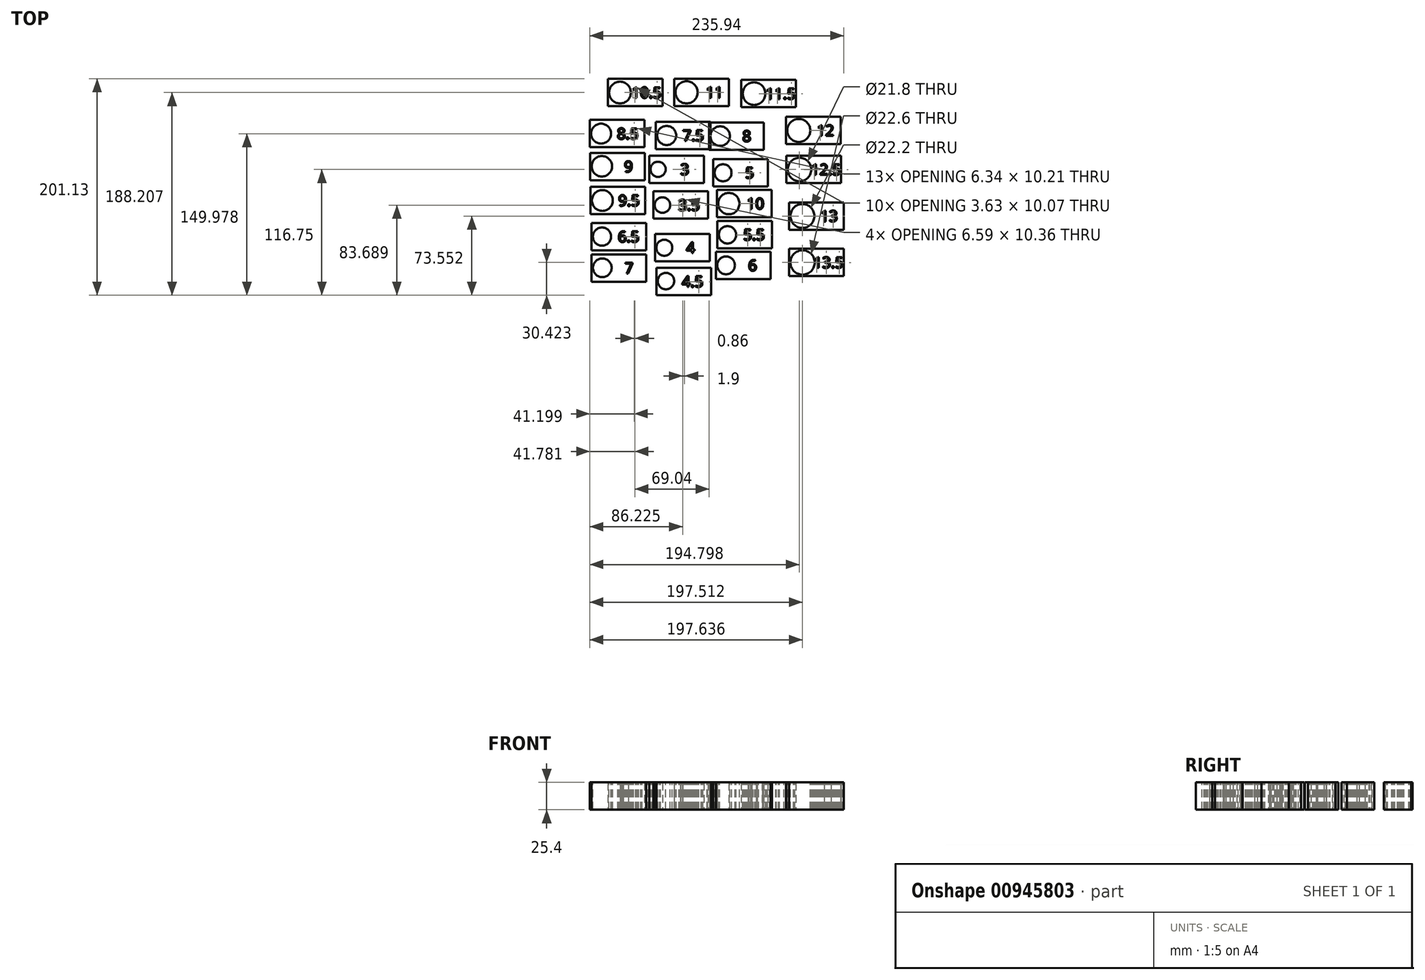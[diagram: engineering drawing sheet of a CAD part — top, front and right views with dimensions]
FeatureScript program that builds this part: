
annotation { "Feature Type Name" : "Feature", "Feature Type Description" : "" }
export const myFeature = defineFeature(function(context is Context, id is Id, definition is map)
    precondition{}
    {
        {
            var Q0;
            Q0=makeQuery(id+"FK1q33cBMZMaRjc_2.opExtrude","CAP_FACE",FACE,{"disambiguationData":[OSD([sQuery(id+"Ff8Uq9xGrrkUuTS_2.wireOp",EDGE,"LQ6pOcAo-RqI5-iYAm-z19J-XkjqRddOA0Lw.bottom"),sQuery(id+"Ff8Uq9xGrrkUuTS_2.wireOp",EDGE,"LQ6pOcAo-RqI5-iYAm-z19J-XkjqRddOA0Lw.top"),sQuery(id+"Ff8Uq9xGrrkUuTS_2.wireOp",EDGE,"LQ6pOcAo-RqI5-iYAm-z19J-XkjqRddOA0Lw.left"),sQuery(id+"Ff8Uq9xGrrkUuTS_2.wireOp",EDGE,"LQ6pOcAo-RqI5-iYAm-z19J-XkjqRddOA0Lw.right")])],"isStart":false});
            var sketch = newSketch(context, id + "F0", { "sketchPlane" : qUnion([Q0])});
            skText(sketch, "E0", { "text": "4", "fontName": "OpenSans-Regular.ttf"});
            const initialGuessF0  = {"E0": [-0.04926, -0.00195, 1, 0, 0.01413]};
            skSetInitialGuess(sketch, initialGuessF0);
            skSolve(sketch);
        }
        {
            var Q0;
            Q0=qCreatedBy(makeId("Top.planeOp"),FACE);
            var sketch = newSketch(context, id + "F1", { "sketchPlane" : qUnion([Q0])});
            skLineSegment(sketch, "E1.bottom", {"start": v(-19.08, 51.73) * mm, "end": v(31.72, 51.73) * mm});
            skLineSegment(sketch, "E1.top", {"start": v(-19.08, 26.33) * mm, "end": v(31.72, 26.33) * mm});
            skLineSegment(sketch, "E1.left", {"start": v(-19.08, 51.73) * mm, "end": v(-19.08, 26.33) * mm});
            skLineSegment(sketch, "E1.right", {"start": v(31.72, 51.73) * mm, "end": v(31.72, 26.33) * mm});
            skSolve(sketch);
        }
        {
            var Q0;
            Q0=qCreatedBy(makeId("Top.planeOp"),FACE);
            var sketch = newSketch(context, id + "F2", { "sketchPlane" : qUnion([Q0])});
            skLineSegment(sketch, "E2.bottom", {"start": v(-15.26, 18.54) * mm, "end": v(35.54, 18.54) * mm});
            skLineSegment(sketch, "E2.top", {"start": v(-15.26, -6.86) * mm, "end": v(35.54, -6.86) * mm});
            skLineSegment(sketch, "E2.left", {"start": v(-15.26, 18.54) * mm, "end": v(-15.26, -6.86) * mm});
            skLineSegment(sketch, "E2.right", {"start": v(35.54, 18.54) * mm, "end": v(35.54, -6.86) * mm});
            skSolve(sketch);
        }
        {
            var Q0;
            Q0=qCreatedBy(makeId("Top.planeOp"),FACE);
            var sketch = newSketch(context, id + "F3", { "sketchPlane" : qUnion([Q0])});
            skLineSegment(sketch, "E3.bottom", {"start": v(-13.72, -20.97) * mm, "end": v(37.08, -20.97) * mm});
            skLineSegment(sketch, "E3.top", {"start": v(-13.72, -46.37) * mm, "end": v(37.08, -46.37) * mm});
            skLineSegment(sketch, "E3.left", {"start": v(-13.72, -20.97) * mm, "end": v(-13.72, -46.37) * mm});
            skLineSegment(sketch, "E3.right", {"start": v(37.08, -20.97) * mm, "end": v(37.08, -46.37) * mm});
            skSolve(sketch);
        }
        {
            var Q0;
            Q0=qCreatedBy(makeId("Top.planeOp"),FACE);
            var sketch = newSketch(context, id + "F4", { "sketchPlane" : qUnion([Q0])});
            skLineSegment(sketch, "E4.bottom", {"start": v(-12.42, -52.5) * mm, "end": v(38.38, -52.5) * mm});
            skLineSegment(sketch, "E4.top", {"start": v(-12.42, -77.9) * mm, "end": v(38.38, -77.9) * mm});
            skLineSegment(sketch, "E4.left", {"start": v(-12.42, -52.5) * mm, "end": v(-12.42, -77.9) * mm});
            skLineSegment(sketch, "E4.right", {"start": v(38.38, -52.5) * mm, "end": v(38.38, -77.9) * mm});
            skSolve(sketch);
        }
        {
            var Q0;
            Q0=qCreatedBy(makeId("Top.planeOp"),FACE);
            var sketch = newSketch(context, id + "F5", { "sketchPlane" : qUnion([Q0])});
            skLineSegment(sketch, "E5.bottom", {"start": v(40.46, 48.55) * mm, "end": v(91.26, 48.55) * mm});
            skLineSegment(sketch, "E5.top", {"start": v(40.46, 23.15) * mm, "end": v(91.26, 23.15) * mm});
            skLineSegment(sketch, "E5.left", {"start": v(40.46, 48.55) * mm, "end": v(40.46, 23.15) * mm});
            skLineSegment(sketch, "E5.right", {"start": v(91.26, 48.55) * mm, "end": v(91.26, 23.15) * mm});
            skSolve(sketch);
        }
        {
            var Q0;
            Q0=qCreatedBy(makeId("Top.planeOp"),FACE);
            var sketch = newSketch(context, id + "F6", { "sketchPlane" : qUnion([Q0])});
            skLineSegment(sketch, "E6.bottom", {"start": v(44.33, -8.99) * mm, "end": v(95.13, -8.99) * mm});
            skLineSegment(sketch, "E6.top", {"start": v(44.33, -34.39) * mm, "end": v(95.13, -34.39) * mm});
            skLineSegment(sketch, "E6.left", {"start": v(44.33, -8.99) * mm, "end": v(44.33, -34.39) * mm});
            skLineSegment(sketch, "E6.right", {"start": v(95.13, -8.99) * mm, "end": v(95.13, -34.39) * mm});
            skSolve(sketch);
        }
        {
            var Q0;
            Q0=qCreatedBy(makeId("Top.planeOp"),FACE);
            var sketch = newSketch(context, id + "F7", { "sketchPlane" : qUnion([Q0])});
            skLineSegment(sketch, "E7.bottom", {"start": v(42.82, -37.42) * mm, "end": v(93.62, -37.42) * mm});
            skLineSegment(sketch, "E7.top", {"start": v(42.82, -62.82) * mm, "end": v(93.62, -62.82) * mm});
            skLineSegment(sketch, "E7.left", {"start": v(42.82, -37.42) * mm, "end": v(42.82, -62.82) * mm});
            skLineSegment(sketch, "E7.right", {"start": v(93.62, -37.42) * mm, "end": v(93.62, -62.82) * mm});
            skSolve(sketch);
        }
        {
            var Q0;
            Q0=makeQuery(id+"F1.imprint","IMPRINT",FACE,{"disambiguationData":[TD([[makeQuery(id+"F1.imprint","IMPRINT",EDGE,{"derivedFrom":sQuery(id+"F1.wireOp",EDGE,"E1.bottom")}),-1.0]])]});
            extrude(context, id + "F8", {"entities" : qUnion([Q0]), "depth" : 25.4 * mm, "offsetDistance" : 25.4 * mm});
        }
        {
            var Q0;
            Q0=makeQuery(id+"F5.imprint","IMPRINT",FACE,{"disambiguationData":[TD([[makeQuery(id+"F5.imprint","IMPRINT",EDGE,{"derivedFrom":sQuery(id+"F5.wireOp",EDGE,"E5.bottom")}),-1.0]])]});
            extrude(context, id + "F9", {"entities" : qUnion([Q0]), "depth" : 25.4 * mm, "offsetDistance" : 25.4 * mm});
        }
        {
            var Q0;
            Q0=makeQuery(id+"F2.imprint","IMPRINT",FACE,{"disambiguationData":[TD([[makeQuery(id+"F2.imprint","IMPRINT",EDGE,{"derivedFrom":sQuery(id+"F2.wireOp",EDGE,"E2.bottom")}),-1.0]])]});
            extrude(context, id + "F10", {"entities" : qUnion([Q0]), "depth" : 25.4 * mm, "offsetDistance" : 25.4 * mm});
        }
        {
            var Q0;
            Q0=makeQuery(id+"F6.imprint","IMPRINT",FACE,{"disambiguationData":[TD([[makeQuery(id+"F6.imprint","IMPRINT",EDGE,{"derivedFrom":sQuery(id+"F6.wireOp",EDGE,"E6.bottom")}),-1.0]])]});
            extrude(context, id + "F11", {"entities" : qUnion([Q0]), "depth" : 25.4 * mm, "offsetDistance" : 25.4 * mm});
        }
        {
            var Q0;
            Q0=makeQuery(id+"F3.imprint","IMPRINT",FACE,{"disambiguationData":[TD([[makeQuery(id+"F3.imprint","IMPRINT",EDGE,{"derivedFrom":sQuery(id+"F3.wireOp",EDGE,"E3.bottom")}),-1.0]])]});
            extrude(context, id + "F12", {"entities" : qUnion([Q0]), "depth" : 25.4 * mm, "offsetDistance" : 25.4 * mm});
        }
        {
            var Q0;
            Q0=makeQuery(id+"F7.imprint","IMPRINT",FACE,{"disambiguationData":[TD([[makeQuery(id+"F7.imprint","IMPRINT",EDGE,{"derivedFrom":sQuery(id+"F7.wireOp",EDGE,"E7.bottom")}),-1.0]])]});
            extrude(context, id + "F13", {"entities" : qUnion([Q0]), "depth" : 25.4 * mm, "offsetDistance" : 25.4 * mm});
        }
        {
            var Q0;
            Q0=makeQuery(id+"F4.imprint","IMPRINT",FACE,{"disambiguationData":[TD([[makeQuery(id+"F4.imprint","IMPRINT",EDGE,{"derivedFrom":sQuery(id+"F4.wireOp",EDGE,"E4.bottom")}),-1.0]])]});
            extrude(context, id + "F14", {"entities" : qUnion([Q0]), "depth" : 25.4 * mm, "offsetDistance" : 25.4 * mm});
        }
        {
            var Q0;
            Q0=makeQuery(id+"F8.opExtrude","CAP_FACE",FACE,{"disambiguationData":[OSD([sQuery(id+"F1.wireOp",EDGE,"E1.bottom"),sQuery(id+"F1.wireOp",EDGE,"E1.top"),sQuery(id+"F1.wireOp",EDGE,"E1.left"),sQuery(id+"F1.wireOp",EDGE,"E1.right")])],"isStart":false});
            var sketch = newSketch(context, id + "F15", { "sketchPlane" : qUnion([Q0])});
            skCircle(sketch, "E8", {"center": v(-10.76, 39.03) * mm, "radius": 7.05 * mm});
            skSolve(sketch);
        }
        {
            var Q0;
            Q0=makeQuery(id+"F15.imprint","IMPRINT",FACE,{"disambiguationData":[TD([[makeQuery(id+"F15.imprint","IMPRINT",EDGE,{"derivedFrom":sQuery(id+"F15.wireOp",EDGE,"E8")}),1.0]])]});
            extrude(context, id + "F16", {"entities" : qUnion([Q0]), "operationType" : NewBodyOperationType.REMOVE, "oppositeDirection" : true, "depth" : 25.4 * mm, "offsetDistance" : 25.4 * mm});
        }
        {
            var Q0;
            Q0=makeQuery(id+"F8.opExtrude","CAP_FACE",FACE,{"disambiguationData":[OSD([sQuery(id+"F1.wireOp",EDGE,"E1.bottom"),sQuery(id+"F1.wireOp",EDGE,"E1.top"),sQuery(id+"F1.wireOp",EDGE,"E1.left"),sQuery(id+"F1.wireOp",EDGE,"E1.right")])],"isStart":false});
            var sketch = newSketch(context, id + "F17", { "sketchPlane" : qUnion([Q0])});
            skText(sketch, "E9", { "text": "3", "fontName": "OpenSans-Regular.ttf"});
            const initialGuessF17  = {"E9": [0.00993, 0.03395, 1, 0, 0.01016]};
            skSetInitialGuess(sketch, initialGuessF17);
            skSolve(sketch);
        }
        {
            var Q0;
            Q0=makeQuery(id+"F17.imprint","IMPRINT",FACE,{"disambiguationData":[TD([[makeQuery(id+"F17.imprint","IMPRINT",EDGE,{"derivedFrom":sQuery(id+"F17.wireOp",EDGE,"E9.sketch_text.stroke-0")}),-1.0]])]});
            extrude(context, id + "F18", {"entities" : qUnion([Q0]), "operationType" : NewBodyOperationType.REMOVE, "oppositeDirection" : true, "depth" : 25.4 * mm, "offsetDistance" : 25.4 * mm});
        }
        {
            var Q0;
            Q0=makeQuery(id+"F10.opExtrude","CAP_FACE",FACE,{"disambiguationData":[OSD([sQuery(id+"F2.wireOp",EDGE,"E2.bottom"),sQuery(id+"F2.wireOp",EDGE,"E2.top"),sQuery(id+"F2.wireOp",EDGE,"E2.left"),sQuery(id+"F2.wireOp",EDGE,"E2.right")])],"isStart":false});
            var sketch = newSketch(context, id + "F19", { "sketchPlane" : qUnion([Q0])});
            skCircle(sketch, "E10", {"center": v(-6.74, 5.84) * mm, "radius": 7.25 * mm});
            skSolve(sketch);
        }
        {
            var Q0;
            Q0=makeQuery(id+"F19.imprint","IMPRINT",FACE,{"disambiguationData":[TD([[makeQuery(id+"F19.imprint","IMPRINT",EDGE,{"derivedFrom":sQuery(id+"F19.wireOp",EDGE,"E10")}),1.0]])]});
            extrude(context, id + "F20", {"entities" : qUnion([Q0]), "operationType" : NewBodyOperationType.REMOVE, "oppositeDirection" : true, "depth" : 25.4 * mm, "offsetDistance" : 25.4 * mm});
        }
        {
            var Q0;
            Q0=makeQuery(id+"F10.opExtrude","CAP_FACE",FACE,{"disambiguationData":[OSD([sQuery(id+"F2.wireOp",EDGE,"E2.bottom"),sQuery(id+"F2.wireOp",EDGE,"E2.top"),sQuery(id+"F2.wireOp",EDGE,"E2.left"),sQuery(id+"F2.wireOp",EDGE,"E2.right")])],"isStart":false});
            var sketch = newSketch(context, id + "F21", { "sketchPlane" : qUnion([Q0])});
            skText(sketch, "E11", { "text": "3.5", "fontName": "OpenSans-Regular.ttf"});
            const initialGuessF21  = {"E11": [0.00803, 0.00076, 1, 0, 0.01016]};
            skSetInitialGuess(sketch, initialGuessF21);
            skSolve(sketch);
        }
        {
            var Q0;
            Q0 = qSketchRegion(id + "F21", true);
            extrude(context, id + "F22", {"entities" : qUnion([Q0]), "operationType" : NewBodyOperationType.REMOVE, "oppositeDirection" : true, "depth" : 25.4 * mm, "offsetDistance" : 25.4 * mm});
        }
        {
            var Q0;
            Q0=makeQuery(id+"F12.opExtrude","CAP_FACE",FACE,{"disambiguationData":[OSD([sQuery(id+"F3.wireOp",EDGE,"E3.bottom"),sQuery(id+"F3.wireOp",EDGE,"E3.top"),sQuery(id+"F3.wireOp",EDGE,"E3.left"),sQuery(id+"F3.wireOp",EDGE,"E3.right")])],"isStart":false});
            var sketch = newSketch(context, id + "F23", { "sketchPlane" : qUnion([Q0])});
            skCircle(sketch, "E12", {"center": v(-5, -33.82) * mm, "radius": 7.45 * mm});
            skSolve(sketch);
        }
        {
            var Q0;
            Q0=makeQuery(id+"F23.imprint","IMPRINT",FACE,{"disambiguationData":[TD([[makeQuery(id+"F23.imprint","IMPRINT",EDGE,{"derivedFrom":sQuery(id+"F23.wireOp",EDGE,"E12")}),1.0]])]});
            extrude(context, id + "F24", {"entities" : qUnion([Q0]), "operationType" : NewBodyOperationType.REMOVE, "oppositeDirection" : true, "depth" : 25.4 * mm, "offsetDistance" : 25.4 * mm});
        }
        {
            var Q0;
            Q0=makeQuery(id+"F12.opExtrude","CAP_FACE",FACE,{"disambiguationData":[OSD([sQuery(id+"F3.wireOp",EDGE,"E3.bottom"),sQuery(id+"F3.wireOp",EDGE,"E3.top"),sQuery(id+"F3.wireOp",EDGE,"E3.left"),sQuery(id+"F3.wireOp",EDGE,"E3.right")])],"isStart":false});
            var sketch = newSketch(context, id + "F25", { "sketchPlane" : qUnion([Q0])});
            skText(sketch, "E13", { "text": "4", "fontName": "OpenSans-Regular.ttf"});
            const initialGuessF25  = {"E13": [0.0154, -0.03875, 1, 0, 0.01016]};
            skSetInitialGuess(sketch, initialGuessF25);
            skSolve(sketch);
        }
        {
            var Q0;
            Q0=makeQuery(id+"F25.imprint","IMPRINT",FACE,{"disambiguationData":[TD([[makeQuery(id+"F25.imprint","IMPRINT",EDGE,{"derivedFrom":sQuery(id+"F25.wireOp",EDGE,"E13.sketch_text.stroke-0")}),-1.0]])]});
            extrude(context, id + "F26", {"entities" : qUnion([Q0]), "operationType" : NewBodyOperationType.REMOVE, "oppositeDirection" : true, "depth" : 25.4 * mm, "offsetDistance" : 25.4 * mm});
        }
        {
            var Q0;
            Q0=makeQuery(id+"F14.opExtrude","CAP_FACE",FACE,{"disambiguationData":[OSD([sQuery(id+"F4.wireOp",EDGE,"E4.bottom"),sQuery(id+"F4.wireOp",EDGE,"E4.top"),sQuery(id+"F4.wireOp",EDGE,"E4.left"),sQuery(id+"F4.wireOp",EDGE,"E4.right")])],"isStart":false});
            var sketch = newSketch(context, id + "F27", { "sketchPlane" : qUnion([Q0])});
            skCircle(sketch, "E14", {"center": v(-3.5, -64.73) * mm, "radius": 7.65 * mm});
            skSolve(sketch);
        }
        {
            var Q0;
            Q0=makeQuery(id+"F27.imprint","IMPRINT",FACE,{"disambiguationData":[TD([[makeQuery(id+"F27.imprint","IMPRINT",EDGE,{"derivedFrom":sQuery(id+"F27.wireOp",EDGE,"E14")}),1.0]])]});
            extrude(context, id + "F28", {"entities" : qUnion([Q0]), "operationType" : NewBodyOperationType.REMOVE, "oppositeDirection" : true, "depth" : 25.4 * mm, "offsetDistance" : 25.4 * mm});
        }
        {
            var Q0;
            Q0=makeQuery(id+"F14.opExtrude","CAP_FACE",FACE,{"disambiguationData":[OSD([sQuery(id+"F4.wireOp",EDGE,"E4.bottom"),sQuery(id+"F4.wireOp",EDGE,"E4.top"),sQuery(id+"F4.wireOp",EDGE,"E4.left"),sQuery(id+"F4.wireOp",EDGE,"E4.right")])],"isStart":false});
            var sketch = newSketch(context, id + "F29", { "sketchPlane" : qUnion([Q0])});
            skText(sketch, "E15", { "text": "4.5", "fontName": "OpenSans-Regular.ttf"});
            const initialGuessF29  = {"E15": [0.01127, -0.07027, 1, 0, 0.01016]};
            skSetInitialGuess(sketch, initialGuessF29);
            skSolve(sketch);
        }
        {
            var Q0;
            Q0 = qSketchRegion(id + "F29", true);
            extrude(context, id + "F30", {"entities" : qUnion([Q0]), "operationType" : NewBodyOperationType.REMOVE, "oppositeDirection" : true, "depth" : 25.4 * mm, "offsetDistance" : 25.4 * mm});
        }
        {
            var Q0;
            Q0=makeQuery(id+"F9.opExtrude","CAP_FACE",FACE,{"disambiguationData":[OSD([sQuery(id+"F5.wireOp",EDGE,"E5.bottom"),sQuery(id+"F5.wireOp",EDGE,"E5.top"),sQuery(id+"F5.wireOp",EDGE,"E5.left"),sQuery(id+"F5.wireOp",EDGE,"E5.right")])],"isStart":false});
            var sketch = newSketch(context, id + "F31", { "sketchPlane" : qUnion([Q0])});
            skCircle(sketch, "E16", {"center": v(49.58, 35.83) * mm, "radius": 7.85 * mm});
            skSolve(sketch);
        }
        {
            var Q0;
            Q0=makeQuery(id+"F31.imprint","IMPRINT",FACE,{"disambiguationData":[TD([[makeQuery(id+"F31.imprint","IMPRINT",EDGE,{"derivedFrom":sQuery(id+"F31.wireOp",EDGE,"E16")}),1.0]])]});
            extrude(context, id + "F32", {"entities" : qUnion([Q0]), "operationType" : NewBodyOperationType.REMOVE, "oppositeDirection" : true, "depth" : 25.4 * mm, "offsetDistance" : 25.4 * mm});
        }
        {
            var Q0;
            Q0=makeQuery(id+"F9.opExtrude","CAP_FACE",FACE,{"disambiguationData":[OSD([sQuery(id+"F5.wireOp",EDGE,"E5.bottom"),sQuery(id+"F5.wireOp",EDGE,"E5.top"),sQuery(id+"F5.wireOp",EDGE,"E5.left"),sQuery(id+"F5.wireOp",EDGE,"E5.right")])],"isStart":false});
            var sketch = newSketch(context, id + "F33", { "sketchPlane" : qUnion([Q0])});
            skText(sketch, "E17", { "text": "5", "fontName": "OpenSans-Regular.ttf"});
            const initialGuessF33  = {"E17": [0.07013, 0.03077, 1, 0, 0.01016]};
            skSetInitialGuess(sketch, initialGuessF33);
            skSolve(sketch);
        }
        {
            var Q0;
            Q0 = qSketchRegion(id + "F33", true);
            extrude(context, id + "F34", {"entities" : qUnion([Q0]), "operationType" : NewBodyOperationType.REMOVE, "oppositeDirection" : true, "depth" : 25.4 * mm, "offsetDistance" : 25.4 * mm});
        }
        {
            var Q0;
            Q0=makeQuery(id+"F11.opExtrude","CAP_FACE",FACE,{"disambiguationData":[OSD([sQuery(id+"F6.wireOp",EDGE,"E6.bottom"),sQuery(id+"F6.wireOp",EDGE,"E6.top"),sQuery(id+"F6.wireOp",EDGE,"E6.left"),sQuery(id+"F6.wireOp",EDGE,"E6.right")])],"isStart":false});
            var sketch = newSketch(context, id + "F35", { "sketchPlane" : qUnion([Q0])});
            skCircle(sketch, "E18", {"center": v(53.65, -21.76) * mm, "radius": 8.05 * mm});
            skSolve(sketch);
        }
        {
            var Q0;
            Q0=makeQuery(id+"F35.imprint","IMPRINT",FACE,{"disambiguationData":[TD([[makeQuery(id+"F35.imprint","IMPRINT",EDGE,{"derivedFrom":sQuery(id+"F35.wireOp",EDGE,"E18")}),1.0]])]});
            extrude(context, id + "F36", {"entities" : qUnion([Q0]), "operationType" : NewBodyOperationType.REMOVE, "oppositeDirection" : true, "depth" : 25.4 * mm, "offsetDistance" : 25.4 * mm});
        }
        {
            var Q0;
            Q0=makeQuery(id+"F11.opExtrude","CAP_FACE",FACE,{"disambiguationData":[OSD([sQuery(id+"F6.wireOp",EDGE,"E6.bottom"),sQuery(id+"F6.wireOp",EDGE,"E6.top"),sQuery(id+"F6.wireOp",EDGE,"E6.left"),sQuery(id+"F6.wireOp",EDGE,"E6.right")])],"isStart":false});
            var sketch = newSketch(context, id + "F37", { "sketchPlane" : qUnion([Q0])});
            skText(sketch, "E19", { "text": "5.5\n", "fontName": "OpenSans-Regular.ttf"});
            const initialGuessF37  = {"E19": [0.06842, -0.02677, 1, 0, 0.01016]};
            skSetInitialGuess(sketch, initialGuessF37);
            skSolve(sketch);
        }
        {
            var Q0;
            Q0=makeQuery(id+"F37.imprint","IMPRINT",FACE,{"disambiguationData":[TD([[makeQuery(id+"F37.imprint","IMPRINT",EDGE,{"derivedFrom":sQuery(id+"F37.wireOp",EDGE,"E19.sketch_text.stroke-27")}),-1.0]])]});
            var Q1;
            Q1 = qSketchRegion(id + "F37", true);
            extrude(context, id + "F38", {"entities" : qUnion([Q0, Q1]), "operationType" : NewBodyOperationType.REMOVE, "oppositeDirection" : true, "depth" : 25.4 * mm, "offsetDistance" : 25.4 * mm});
        }
        {
            var Q0;
            Q0=makeQuery(id+"F13.opExtrude","CAP_FACE",FACE,{"disambiguationData":[OSD([sQuery(id+"F7.wireOp",EDGE,"E7.bottom"),sQuery(id+"F7.wireOp",EDGE,"E7.top"),sQuery(id+"F7.wireOp",EDGE,"E7.left"),sQuery(id+"F7.wireOp",EDGE,"E7.right")])],"isStart":false});
            var sketch = newSketch(context, id + "F39", { "sketchPlane" : qUnion([Q0])});
            skCircle(sketch, "E20", {"center": v(52.34, -50.13) * mm, "radius": 8.25 * mm});
            skSolve(sketch);
        }
        {
            var Q0;
            Q0=makeQuery(id+"F39.imprint","IMPRINT",FACE,{"disambiguationData":[TD([[makeQuery(id+"F39.imprint","IMPRINT",EDGE,{"derivedFrom":sQuery(id+"F39.wireOp",EDGE,"E20")}),1.0]])]});
            extrude(context, id + "F40", {"entities" : qUnion([Q0]), "operationType" : NewBodyOperationType.REMOVE, "oppositeDirection" : true, "depth" : 25.4 * mm, "offsetDistance" : 25.4 * mm});
        }
        {
            var Q0;
            Q0=makeQuery(id+"F13.opExtrude","CAP_FACE",FACE,{"disambiguationData":[OSD([sQuery(id+"F7.wireOp",EDGE,"E7.bottom"),sQuery(id+"F7.wireOp",EDGE,"E7.top"),sQuery(id+"F7.wireOp",EDGE,"E7.left"),sQuery(id+"F7.wireOp",EDGE,"E7.right")])],"isStart":false});
            var sketch = newSketch(context, id + "F41", { "sketchPlane" : qUnion([Q0])});
            skText(sketch, "E21", { "text": "6", "fontName": "OpenSans-Regular.ttf"});
            const initialGuessF41  = {"E21": [0.07295, -0.0552, 1, 0, 0.01016]};
            skSetInitialGuess(sketch, initialGuessF41);
            skSolve(sketch);
        }
        {
            var Q0;
            Q0 = qSketchRegion(id + "F41", true);
            extrude(context, id + "F42", {"entities" : qUnion([Q0]), "operationType" : NewBodyOperationType.REMOVE, "oppositeDirection" : true, "depth" : 25.4 * mm, "offsetDistance" : 25.4 * mm});
        }
        {
            var Q0;
            Q0=qCreatedBy(makeId("Top.planeOp"),FACE);
            var sketch = newSketch(context, id + "F43", { "sketchPlane" : qUnion([Q0])});
            skLineSegment(sketch, "E22.bottom", {"start": v(-72.58, -10.77) * mm, "end": v(-21.78, -10.77) * mm});
            skLineSegment(sketch, "E22.top", {"start": v(-72.58, -36.17) * mm, "end": v(-21.78, -36.17) * mm});
            skLineSegment(sketch, "E22.left", {"start": v(-72.58, -10.77) * mm, "end": v(-72.58, -36.17) * mm});
            skLineSegment(sketch, "E22.right", {"start": v(-21.78, -10.77) * mm, "end": v(-21.78, -36.17) * mm});
            skSolve(sketch);
        }
        {
            var Q0;
            Q0=qCreatedBy(makeId("Top.planeOp"),FACE);
            var sketch = newSketch(context, id + "F44", { "sketchPlane" : qUnion([Q0])});
            skLineSegment(sketch, "E23.bottom", {"start": v(-72.53, -40) * mm, "end": v(-21.73, -40) * mm});
            skLineSegment(sketch, "E23.top", {"start": v(-72.53, -65.4) * mm, "end": v(-21.73, -65.4) * mm});
            skLineSegment(sketch, "E23.left", {"start": v(-72.53, -40) * mm, "end": v(-72.53, -65.4) * mm});
            skLineSegment(sketch, "E23.right", {"start": v(-21.73, -40) * mm, "end": v(-21.73, -65.4) * mm});
            skSolve(sketch);
        }
        {
            var Q0;
            Q0=qCreatedBy(makeId("Top.planeOp"),FACE);
            var sketch = newSketch(context, id + "F45", { "sketchPlane" : qUnion([Q0])});
            skLineSegment(sketch, "E24.bottom", {"start": v(-12.95, 83.2) * mm, "end": v(37.85, 83.2) * mm});
            skLineSegment(sketch, "E24.top", {"start": v(-12.95, 57.8) * mm, "end": v(37.85, 57.8) * mm});
            skLineSegment(sketch, "E24.left", {"start": v(-12.95, 83.2) * mm, "end": v(-12.95, 57.8) * mm});
            skLineSegment(sketch, "E24.right", {"start": v(37.85, 83.2) * mm, "end": v(37.85, 57.8) * mm});
            skSolve(sketch);
        }
        {
            var Q0;
            Q0=qCreatedBy(makeId("Top.planeOp"),FACE);
            var sketch = newSketch(context, id + "F46", { "sketchPlane" : qUnion([Q0])});
            skLineSegment(sketch, "E25.bottom", {"start": v(36.57, 82.63) * mm, "end": v(87.37, 82.63) * mm});
            skLineSegment(sketch, "E25.top", {"start": v(36.57, 57.23) * mm, "end": v(87.37, 57.23) * mm});
            skLineSegment(sketch, "E25.left", {"start": v(36.57, 82.63) * mm, "end": v(36.57, 57.23) * mm});
            skLineSegment(sketch, "E25.right", {"start": v(87.37, 82.63) * mm, "end": v(87.37, 57.23) * mm});
            skSolve(sketch);
        }
        {
            var Q0;
            Q0=makeQuery(id+"F43.imprint","IMPRINT",FACE,{"disambiguationData":[TD([[makeQuery(id+"F43.imprint","IMPRINT",EDGE,{"derivedFrom":sQuery(id+"F43.wireOp",EDGE,"E22.bottom")}),-1.0]])]});
            extrude(context, id + "F47", {"entities" : qUnion([Q0]), "depth" : 25.4 * mm, "offsetDistance" : 25.4 * mm});
        }
        {
            var Q0;
            Q0=makeQuery(id+"F44.imprint","IMPRINT",FACE,{"disambiguationData":[TD([[makeQuery(id+"F44.imprint","IMPRINT",EDGE,{"derivedFrom":sQuery(id+"F44.wireOp",EDGE,"E23.bottom")}),-1.0]])]});
            extrude(context, id + "F48", {"entities" : qUnion([Q0]), "depth" : 25.4 * mm, "offsetDistance" : 25.4 * mm});
        }
        {
            var Q0;
            Q0=makeQuery(id+"F45.imprint","IMPRINT",FACE,{"disambiguationData":[TD([[makeQuery(id+"F45.imprint","IMPRINT",EDGE,{"derivedFrom":sQuery(id+"F45.wireOp",EDGE,"E24.bottom")}),-1.0]])]});
            extrude(context, id + "F49", {"entities" : qUnion([Q0]), "depth" : 25.4 * mm, "offsetDistance" : 25.4 * mm});
        }
        {
            var Q0;
            Q0=makeQuery(id+"F46.imprint","IMPRINT",FACE,{"disambiguationData":[TD([[makeQuery(id+"F46.imprint","IMPRINT",EDGE,{"derivedFrom":sQuery(id+"F46.wireOp",EDGE,"E25.bottom")}),-1.0]])]});
            extrude(context, id + "F50", {"entities" : qUnion([Q0]), "depth" : 25.4 * mm, "offsetDistance" : 25.4 * mm});
        }
        {
            var Q0;
            Q0=makeQuery(id+"F47.opExtrude","CAP_FACE",FACE,{"disambiguationData":[OSD([sQuery(id+"F43.wireOp",EDGE,"E22.bottom"),sQuery(id+"F43.wireOp",EDGE,"E22.top"),sQuery(id+"F43.wireOp",EDGE,"E22.left"),sQuery(id+"F43.wireOp",EDGE,"E22.right")])],"isStart":false});
            var sketch = newSketch(context, id + "F51", { "sketchPlane" : qUnion([Q0])});
            skCircle(sketch, "E26", {"center": v(-62.86, -23.47) * mm, "radius": 8.45 * mm});
            skSolve(sketch);
        }
        {
            var Q0;
            Q0=makeQuery(id+"F51.imprint","IMPRINT",FACE,{"disambiguationData":[TD([[makeQuery(id+"F51.imprint","IMPRINT",EDGE,{"derivedFrom":sQuery(id+"F51.wireOp",EDGE,"E26")}),1.0]])]});
            extrude(context, id + "F52", {"entities" : qUnion([Q0]), "operationType" : NewBodyOperationType.REMOVE, "oppositeDirection" : true, "depth" : 25.4 * mm, "offsetDistance" : 25.4 * mm});
        }
        {
            var Q0;
            Q0=makeQuery(id+"F47.opExtrude","CAP_FACE",FACE,{"disambiguationData":[OSD([sQuery(id+"F43.wireOp",EDGE,"E22.bottom"),sQuery(id+"F43.wireOp",EDGE,"E22.top"),sQuery(id+"F43.wireOp",EDGE,"E22.left"),sQuery(id+"F43.wireOp",EDGE,"E22.right")])],"isStart":false});
            var sketch = newSketch(context, id + "F53", { "sketchPlane" : qUnion([Q0])});
            skText(sketch, "E27", { "text": "6.5", "fontName": "OpenSans-Regular.ttf"});
            const initialGuessF53  = {"E27": [-0.0481, -0.02855, 1, 0, 0.01016]};
            skSetInitialGuess(sketch, initialGuessF53);
            skSolve(sketch);
        }
        {
            var Q0;
            Q0 = qSketchRegion(id + "F53", true);
            extrude(context, id + "F54", {"entities" : qUnion([Q0]), "operationType" : NewBodyOperationType.REMOVE, "oppositeDirection" : true, "depth" : 25.4 * mm, "offsetDistance" : 25.4 * mm});
        }
        {
            var Q0;
            Q0=makeQuery(id+"F48.opExtrude","CAP_FACE",FACE,{"disambiguationData":[OSD([sQuery(id+"F44.wireOp",EDGE,"E23.bottom"),sQuery(id+"F44.wireOp",EDGE,"E23.top"),sQuery(id+"F44.wireOp",EDGE,"E23.left"),sQuery(id+"F44.wireOp",EDGE,"E23.right")])],"isStart":false});
            var sketch = newSketch(context, id + "F55", { "sketchPlane" : qUnion([Q0])});
            skCircle(sketch, "E28", {"center": v(-62.62, -52.42) * mm, "radius": 8.65 * mm});
            skSolve(sketch);
        }
        {
            var Q0;
            Q0=makeQuery(id+"F55.imprint","IMPRINT",FACE,{"disambiguationData":[TD([[makeQuery(id+"F55.imprint","IMPRINT",EDGE,{"derivedFrom":sQuery(id+"F55.wireOp",EDGE,"E28")}),1.0]])]});
            extrude(context, id + "F56", {"entities" : qUnion([Q0]), "operationType" : NewBodyOperationType.REMOVE, "oppositeDirection" : true, "depth" : 25.4 * mm, "offsetDistance" : 25.4 * mm});
        }
        {
            var Q0;
            Q0=makeQuery(id+"F48.opExtrude","CAP_FACE",FACE,{"disambiguationData":[OSD([sQuery(id+"F44.wireOp",EDGE,"E23.bottom"),sQuery(id+"F44.wireOp",EDGE,"E23.top"),sQuery(id+"F44.wireOp",EDGE,"E23.left"),sQuery(id+"F44.wireOp",EDGE,"E23.right")])],"isStart":false});
            var sketch = newSketch(context, id + "F57", { "sketchPlane" : qUnion([Q0])});
            skText(sketch, "E29", { "text": "7", "fontName": "OpenSans-Regular.ttf"});
            const initialGuessF57  = {"E29": [-0.04198, -0.05777, 1, 0, 0.01016]};
            skSetInitialGuess(sketch, initialGuessF57);
            skSolve(sketch);
        }
        {
            var Q0;
            Q0 = qSketchRegion(id + "F57", true);
            extrude(context, id + "F58", {"entities" : qUnion([Q0]), "operationType" : NewBodyOperationType.REMOVE, "oppositeDirection" : true, "depth" : 25.4 * mm, "offsetDistance" : 25.4 * mm});
        }
        {
            var Q0;
            Q0=makeQuery(id+"F49.opExtrude","CAP_FACE",FACE,{"disambiguationData":[OSD([sQuery(id+"F45.wireOp",EDGE,"E24.bottom"),sQuery(id+"F45.wireOp",EDGE,"E24.top"),sQuery(id+"F45.wireOp",EDGE,"E24.left"),sQuery(id+"F45.wireOp",EDGE,"E24.right")])],"isStart":false});
            var sketch = newSketch(context, id + "F59", { "sketchPlane" : qUnion([Q0])});
            skCircle(sketch, "E30", {"center": v(-2.83, 70.46) * mm, "radius": 8.85 * mm});
            skSolve(sketch);
        }
        {
            var Q0;
            Q0=makeQuery(id+"F59.imprint","IMPRINT",FACE,{"disambiguationData":[TD([[makeQuery(id+"F59.imprint","IMPRINT",EDGE,{"derivedFrom":sQuery(id+"F59.wireOp",EDGE,"E30")}),1.0]])]});
            extrude(context, id + "F60", {"entities" : qUnion([Q0]), "operationType" : NewBodyOperationType.ADD, "depth" : 25.4 * mm, "offsetDistance" : 25.4 * mm});
        }
        {
            var Q0;
            Q0=makeQuery(id+"F60.opExtrude","CAP_FACE",FACE,{"disambiguationData":[OSD([sQuery(id+"F59.wireOp",EDGE,"E30")])],"isStart":false});
            extrude(context, id + "F61", {"entities" : qUnion([Q0]), "operationType" : NewBodyOperationType.REMOVE, "oppositeDirection" : true, "depth" : 50.8 * mm, "offsetDistance" : 25.4 * mm});
        }
        {
            var Q0;
            Q0=makeQuery(id+"F49.opExtrude","CAP_FACE",FACE,{"disambiguationData":[OSD([sQuery(id+"F45.wireOp",EDGE,"E24.bottom"),sQuery(id+"F45.wireOp",EDGE,"E24.top"),sQuery(id+"F45.wireOp",EDGE,"E24.left"),sQuery(id+"F45.wireOp",EDGE,"E24.right")])],"isStart":false});
            var sketch = newSketch(context, id + "F62", { "sketchPlane" : qUnion([Q0])});
            skText(sketch, "E31", { "text": "7.5", "fontName": "OpenSans-Regular.ttf"});
            const initialGuessF62  = {"E31": [0.01194, 0.06542, 1, 0, 0.01016]};
            skSetInitialGuess(sketch, initialGuessF62);
            skSolve(sketch);
        }
        {
            var Q0;
            Q0 = qSketchRegion(id + "F62", true);
            extrude(context, id + "F63", {"entities" : qUnion([Q0]), "operationType" : NewBodyOperationType.REMOVE, "oppositeDirection" : true, "depth" : 25.4 * mm, "offsetDistance" : 25.4 * mm});
        }
        {
            var Q0;
            Q0=makeQuery(id+"F50.opExtrude","CAP_FACE",FACE,{"disambiguationData":[OSD([sQuery(id+"F46.wireOp",EDGE,"E25.bottom"),sQuery(id+"F46.wireOp",EDGE,"E25.top"),sQuery(id+"F46.wireOp",EDGE,"E25.left"),sQuery(id+"F46.wireOp",EDGE,"E25.right")])],"isStart":false});
            var sketch = newSketch(context, id + "F64", { "sketchPlane" : qUnion([Q0])});
            skCircle(sketch, "E32", {"center": v(46.9, 69.9) * mm, "radius": 9.05 * mm});
            skSolve(sketch);
        }
        {
            var Q0;
            Q0=makeQuery(id+"F64.imprint","IMPRINT",FACE,{"disambiguationData":[TD([[makeQuery(id+"F64.imprint","IMPRINT",EDGE,{"derivedFrom":sQuery(id+"F64.wireOp",EDGE,"E32")}),1.0]])]});
            extrude(context, id + "F65", {"entities" : qUnion([Q0]), "operationType" : NewBodyOperationType.REMOVE, "oppositeDirection" : true, "depth" : 25.4 * mm, "offsetDistance" : 25.4 * mm});
        }
        {
            var Q0;
            Q0=makeQuery(id+"F50.opExtrude","CAP_FACE",FACE,{"disambiguationData":[OSD([sQuery(id+"F46.wireOp",EDGE,"E25.bottom"),sQuery(id+"F46.wireOp",EDGE,"E25.top"),sQuery(id+"F46.wireOp",EDGE,"E25.left"),sQuery(id+"F46.wireOp",EDGE,"E25.right")])],"isStart":false});
            var sketch = newSketch(context, id + "F66", { "sketchPlane" : qUnion([Q0])});
            skText(sketch, "E33", { "text": "8", "fontName": "OpenSans-Regular.ttf"});
            const initialGuessF66  = {"E33": [0.06751, 0.06485, 1, 0, 0.01016]};
            skSetInitialGuess(sketch, initialGuessF66);
            skSolve(sketch);
        }
        {
            var Q0;
            Q0=makeQuery(id+"F66.imprint","IMPRINT",FACE,{"disambiguationData":[TD([[makeQuery(id+"F66.imprint","IMPRINT",EDGE,{"derivedFrom":sQuery(id+"F66.wireOp",EDGE,"E33.sketch_text.stroke-0")}),-1.0]])]});
            extrude(context, id + "F67", {"entities" : qUnion([Q0]), "operationType" : NewBodyOperationType.REMOVE, "oppositeDirection" : true, "depth" : 25.4 * mm, "offsetDistance" : 25.4 * mm});
        }
        {
            var Q0;
            Q0=qCreatedBy(makeId("Top.planeOp"),FACE);
            var sketch = newSketch(context, id + "F68", { "sketchPlane" : qUnion([Q0])});
            skLineSegment(sketch, "E34.bottom", {"start": v(-74.25, 84.9) * mm, "end": v(-23.45, 84.9) * mm});
            skLineSegment(sketch, "E34.top", {"start": v(-74.25, 59.5) * mm, "end": v(-23.45, 59.5) * mm});
            skLineSegment(sketch, "E34.left", {"start": v(-74.25, 84.9) * mm, "end": v(-74.25, 59.5) * mm});
            skLineSegment(sketch, "E34.right", {"start": v(-23.45, 84.9) * mm, "end": v(-23.45, 59.5) * mm});
            skSolve(sketch);
        }
        {
            var Q0;
            Q0=qCreatedBy(makeId("Top.planeOp"),FACE);
            var sketch = newSketch(context, id + "F69", { "sketchPlane" : qUnion([Q0])});
            skLineSegment(sketch, "E35.bottom", {"start": v(-73.78, 54.3) * mm, "end": v(-22.98, 54.3) * mm});
            skLineSegment(sketch, "E35.top", {"start": v(-73.78, 28.9) * mm, "end": v(-22.98, 28.9) * mm});
            skLineSegment(sketch, "E35.left", {"start": v(-73.78, 54.3) * mm, "end": v(-73.78, 28.9) * mm});
            skLineSegment(sketch, "E35.right", {"start": v(-22.98, 54.3) * mm, "end": v(-22.98, 28.9) * mm});
            skSolve(sketch);
        }
        {
            var Q0;
            Q0=qCreatedBy(makeId("Top.planeOp"),FACE);
            var sketch = newSketch(context, id + "F70", { "sketchPlane" : qUnion([Q0])});
            skLineSegment(sketch, "E36.bottom", {"start": v(-73.54, 22.78) * mm, "end": v(-22.74, 22.78) * mm});
            skLineSegment(sketch, "E36.top", {"start": v(-73.54, -2.62) * mm, "end": v(-22.74, -2.62) * mm});
            skLineSegment(sketch, "E36.left", {"start": v(-73.54, 22.78) * mm, "end": v(-73.54, -2.62) * mm});
            skLineSegment(sketch, "E36.right", {"start": v(-22.74, 22.78) * mm, "end": v(-22.74, -2.62) * mm});
            skSolve(sketch);
        }
        {
            var Q0;
            Q0=qCreatedBy(makeId("Top.planeOp"),FACE);
            var sketch = newSketch(context, id + "F71", { "sketchPlane" : qUnion([Q0])});
            skLineSegment(sketch, "E37.bottom", {"start": v(43.73, 19.92) * mm, "end": v(94.53, 19.92) * mm});
            skLineSegment(sketch, "E37.top", {"start": v(43.73, -5.48) * mm, "end": v(94.53, -5.48) * mm});
            skLineSegment(sketch, "E37.left", {"start": v(43.73, 19.92) * mm, "end": v(43.73, -5.48) * mm});
            skLineSegment(sketch, "E37.right", {"start": v(94.53, 19.92) * mm, "end": v(94.53, -5.48) * mm});
            skSolve(sketch);
        }
        {
            var Q0;
            Q0=makeQuery(id+"F68.imprint","IMPRINT",FACE,{"disambiguationData":[TD([[makeQuery(id+"F68.imprint","IMPRINT",EDGE,{"derivedFrom":sQuery(id+"F68.wireOp",EDGE,"E34.bottom")}),-1.0]])]});
            extrude(context, id + "F72", {"entities" : qUnion([Q0]), "depth" : 25.4 * mm, "offsetDistance" : 25.4 * mm});
        }
        {
            var Q0;
            Q0=makeQuery(id+"F69.imprint","IMPRINT",FACE,{"disambiguationData":[TD([[makeQuery(id+"F69.imprint","IMPRINT",EDGE,{"derivedFrom":sQuery(id+"F69.wireOp",EDGE,"E35.bottom")}),-1.0]])]});
            extrude(context, id + "F73", {"entities" : qUnion([Q0]), "depth" : 25.4 * mm, "offsetDistance" : 25.4 * mm});
        }
        {
            var Q0;
            Q0=makeQuery(id+"F70.imprint","IMPRINT",FACE,{"disambiguationData":[TD([[makeQuery(id+"F70.imprint","IMPRINT",EDGE,{"derivedFrom":sQuery(id+"F70.wireOp",EDGE,"E36.bottom")}),-1.0]])]});
            extrude(context, id + "F74", {"entities" : qUnion([Q0]), "depth" : 25.4 * mm, "offsetDistance" : 25.4 * mm});
        }
        {
            var Q0;
            Q0=makeQuery(id+"F71.imprint","IMPRINT",FACE,{"disambiguationData":[TD([[makeQuery(id+"F71.imprint","IMPRINT",EDGE,{"derivedFrom":sQuery(id+"F71.wireOp",EDGE,"E37.bottom")}),-1.0]])]});
            extrude(context, id + "F75", {"entities" : qUnion([Q0]), "depth" : 25.4 * mm, "offsetDistance" : 25.4 * mm});
        }
        {
            var Q0;
            Q0=makeQuery(id+"F72.opExtrude","CAP_FACE",FACE,{"disambiguationData":[OSD([sQuery(id+"F68.wireOp",EDGE,"E34.bottom"),sQuery(id+"F68.wireOp",EDGE,"E34.top"),sQuery(id+"F68.wireOp",EDGE,"E34.left"),sQuery(id+"F68.wireOp",EDGE,"E34.right")])],"isStart":false});
            var sketch = newSketch(context, id + "F76", { "sketchPlane" : qUnion([Q0])});
            skCircle(sketch, "E38", {"center": v(-63.73, 72.2) * mm, "radius": 9.25 * mm});
            skSolve(sketch);
        }
        {
            var Q0;
            Q0=makeQuery(id+"F76.imprint","IMPRINT",FACE,{"disambiguationData":[TD([[makeQuery(id+"F76.imprint","IMPRINT",EDGE,{"derivedFrom":sQuery(id+"F76.wireOp",EDGE,"E38")}),1.0]])]});
            extrude(context, id + "F77", {"entities" : qUnion([Q0]), "operationType" : NewBodyOperationType.REMOVE, "oppositeDirection" : true, "depth" : 25.4 * mm, "offsetDistance" : 25.4 * mm});
        }
        {
            var Q0;
            Q0=makeQuery(id+"F72.opExtrude","CAP_FACE",FACE,{"disambiguationData":[OSD([sQuery(id+"F68.wireOp",EDGE,"E34.bottom"),sQuery(id+"F68.wireOp",EDGE,"E34.top"),sQuery(id+"F68.wireOp",EDGE,"E34.left"),sQuery(id+"F68.wireOp",EDGE,"E34.right")])],"isStart":false});
            var sketch = newSketch(context, id + "F78", { "sketchPlane" : qUnion([Q0])});
            skText(sketch, "E39", { "text": "8.5", "fontName": "OpenSans-Regular.ttf"});
            const initialGuessF78  = {"E39": [-0.04896, 0.06712, 1, 0, 0.01016]};
            skSetInitialGuess(sketch, initialGuessF78);
            skSolve(sketch);
        }
        {
            var Q0;
            Q0=makeQuery(id+"F73.opExtrude","CAP_FACE",FACE,{"disambiguationData":[OSD([sQuery(id+"F69.wireOp",EDGE,"E35.bottom"),sQuery(id+"F69.wireOp",EDGE,"E35.top"),sQuery(id+"F69.wireOp",EDGE,"E35.left"),sQuery(id+"F69.wireOp",EDGE,"E35.right")])],"isStart":false});
            var sketch = newSketch(context, id + "F79", { "sketchPlane" : qUnion([Q0])});
            skCircle(sketch, "E40", {"center": v(-63, 41.84) * mm, "radius": 9.5 * mm});
            skSolve(sketch);
        }
        {
            var Q0;
            Q0=makeQuery(id+"F79.imprint","IMPRINT",FACE,{"disambiguationData":[TD([[makeQuery(id+"F79.imprint","IMPRINT",EDGE,{"derivedFrom":sQuery(id+"F79.wireOp",EDGE,"E40")}),1.0]])]});
            extrude(context, id + "F80", {"entities" : qUnion([Q0]), "operationType" : NewBodyOperationType.REMOVE, "oppositeDirection" : true, "depth" : 25.4 * mm, "offsetDistance" : 25.4 * mm});
        }
        {
            var Q0;
            Q0=makeQuery(id+"F73.opExtrude","CAP_FACE",FACE,{"disambiguationData":[OSD([sQuery(id+"F69.wireOp",EDGE,"E35.bottom"),sQuery(id+"F69.wireOp",EDGE,"E35.top"),sQuery(id+"F69.wireOp",EDGE,"E35.left"),sQuery(id+"F69.wireOp",EDGE,"E35.right")])],"isStart":false});
            var sketch = newSketch(context, id + "F81", { "sketchPlane" : qUnion([Q0])});
            skText(sketch, "E41", { "text": "9", "fontName": "OpenSans-Regular.ttf"});
            const initialGuessF81  = {"E41": [-0.04236, 0.03651, 1, 0, 0.01016]};
            skSetInitialGuess(sketch, initialGuessF81);
            skSolve(sketch);
        }
        {
            var Q0;
            Q0 = qSketchRegion(id + "F81", true);
            extrude(context, id + "F82", {"entities" : qUnion([Q0]), "operationType" : NewBodyOperationType.REMOVE, "oppositeDirection" : true, "depth" : 25.4 * mm, "offsetDistance" : 25.4 * mm});
        }
        {
            var Q0;
            Q0=makeQuery(id+"F75.opExtrude","CAP_FACE",FACE,{"disambiguationData":[OSD([sQuery(id+"F71.wireOp",EDGE,"E37.bottom"),sQuery(id+"F71.wireOp",EDGE,"E37.top"),sQuery(id+"F71.wireOp",EDGE,"E37.left"),sQuery(id+"F71.wireOp",EDGE,"E37.right")])],"isStart":false});
            var sketch = newSketch(context, id + "F83", { "sketchPlane" : qUnion([Q0])});
            skCircle(sketch, "E42", {"center": v(54.9, 7.22) * mm, "radius": 9.9 * mm});
            skSolve(sketch);
        }
        {
            var Q0;
            Q0=makeQuery(id+"F83.imprint","IMPRINT",FACE,{"disambiguationData":[TD([[makeQuery(id+"F83.imprint","IMPRINT",EDGE,{"derivedFrom":sQuery(id+"F83.wireOp",EDGE,"E42")}),1.0]])]});
            var sketch = newSketch(context, id + "F84", { "sketchPlane" : qUnion([Q0])});
            skSolve(sketch);
        }
        {
            var Q0;
            Q0=makeQuery(id+"F84.imprint","IMPRINT",FACE,{"disambiguationData":[TD([[makeQuery(id+"F84.imprint","IMPRINT",EDGE,{"derivedFrom":makeQuery(id+"F83.imprint","IMPRINT",EDGE,{"derivedFrom":sQuery(id+"F83.wireOp",EDGE,"E42")})}),1.0]])]});
            extrude(context, id + "F85", {"entities" : qUnion([Q0]), "operationType" : NewBodyOperationType.REMOVE, "depth" : 25.4 * mm, "offsetDistance" : 25.4 * mm});
        }
        {
            var Q0;
            Q0=makeQuery(id+"F83.imprint","IMPRINT",FACE,{"disambiguationData":[TD([[makeQuery(id+"F83.imprint","IMPRINT",EDGE,{"derivedFrom":sQuery(id+"F83.wireOp",EDGE,"E42")}),1.0]])]});
            extrude(context, id + "F86", {"entities" : qUnion([Q0]), "operationType" : NewBodyOperationType.REMOVE, "oppositeDirection" : true, "depth" : 25.4 * mm, "offsetDistance" : 25.4 * mm});
        }
        {
            var Q0;
            Q0 = qSketchRegion(id + "F78", true);
            extrude(context, id + "F87", {"entities" : qUnion([Q0]), "operationType" : NewBodyOperationType.REMOVE, "oppositeDirection" : true, "depth" : 25.4 * mm, "offsetDistance" : 25.4 * mm});
        }
        {
            var Q0;
            Q0=qCreatedBy(makeId("Top.planeOp"),FACE);
            var sketch = newSketch(context, id + "F88", { "sketchPlane" : qUnion([Q0])});
            skText(sketch, "E43", { "text": "10", "fontName": "OpenSans-Regular.ttf"});
            const initialGuessF88  = {"E43": [0.0715, 0.00214, 1, 0, 0.01016]};
            skSetInitialGuess(sketch, initialGuessF88);
            skSolve(sketch);
        }
        {
            var Q0;
            Q0 = qSketchRegion(id + "F88", true);
            extrude(context, id + "F89", {"entities" : qUnion([Q0]), "operationType" : NewBodyOperationType.REMOVE, "depth" : 25.4 * mm, "offsetDistance" : 25.4 * mm});
        }
        {
            var Q0;
            Q0=makeQuery(id+"F74.opExtrude","CAP_FACE",FACE,{"disambiguationData":[OSD([sQuery(id+"F70.wireOp",EDGE,"E36.bottom"),sQuery(id+"F70.wireOp",EDGE,"E36.top"),sQuery(id+"F70.wireOp",EDGE,"E36.left"),sQuery(id+"F70.wireOp",EDGE,"E36.right")])],"isStart":false});
            var sketch = newSketch(context, id + "F90", { "sketchPlane" : qUnion([Q0])});
            skCircle(sketch, "E44", {"center": v(-62.57, 10.08) * mm, "radius": 9.7 * mm});
            skSolve(sketch);
        }
        {
            var Q0;
            Q0=makeQuery(id+"F90.imprint","IMPRINT",FACE,{"disambiguationData":[TD([[makeQuery(id+"F90.imprint","IMPRINT",EDGE,{"derivedFrom":sQuery(id+"F90.wireOp",EDGE,"E44")}),1.0]])]});
            extrude(context, id + "F91", {"entities" : qUnion([Q0]), "operationType" : NewBodyOperationType.REMOVE, "oppositeDirection" : true, "depth" : 25.4 * mm, "offsetDistance" : 25.4 * mm});
        }
        {
            var Q0;
            Q0=makeQuery(id+"F74.opExtrude","CAP_FACE",FACE,{"disambiguationData":[OSD([sQuery(id+"F70.wireOp",EDGE,"E36.bottom"),sQuery(id+"F70.wireOp",EDGE,"E36.top"),sQuery(id+"F70.wireOp",EDGE,"E36.left"),sQuery(id+"F70.wireOp",EDGE,"E36.right")])],"isStart":false});
            var sketch = newSketch(context, id + "F92", { "sketchPlane" : qUnion([Q0])});
            skText(sketch, "E45", { "text": "9.5\n", "fontName": "OpenSans-Regular.ttf"});
            const initialGuessF92  = {"E45": [-0.04781, 0.005, 1, 0, 0.01016]};
            skSetInitialGuess(sketch, initialGuessF92);
            skSolve(sketch);
        }
        {
            var Q0;
            Q0 = qSketchRegion(id + "F92", true);
            extrude(context, id + "F93", {"entities" : qUnion([Q0]), "operationType" : NewBodyOperationType.REMOVE, "oppositeDirection" : true, "depth" : 25.4 * mm, "offsetDistance" : 25.4 * mm});
        }
        {
            var Q0;
            Q0=qCreatedBy(makeId("Top.planeOp"),FACE);
            var sketch = newSketch(context, id + "F94", { "sketchPlane" : qUnion([Q0])});
            skLineSegment(sketch, "E46.bottom", {"start": v(-57.55, 123.06) * mm, "end": v(-6.75, 123.06) * mm});
            skLineSegment(sketch, "E46.top", {"start": v(-57.55, 97.66) * mm, "end": v(-6.75, 97.66) * mm});
            skLineSegment(sketch, "E46.left", {"start": v(-57.55, 123.06) * mm, "end": v(-57.55, 97.66) * mm});
            skLineSegment(sketch, "E46.right", {"start": v(-6.75, 123.06) * mm, "end": v(-6.75, 97.66) * mm});
            skLineSegment(sketch, "E47.bottom", {"start": v(2.24, 119.29) * mm, "end": v(42.88, 119.29) * mm});
            skLineSegment(sketch, "E47.top", {"start": v(2.24, 93.89) * mm, "end": v(42.88, 93.89) * mm});
            skLineSegment(sketch, "E47.left", {"start": v(2.24, 119.29) * mm, "end": v(2.24, 93.89) * mm});
            skLineSegment(sketch, "E47.right", {"start": v(42.88, 119.29) * mm, "end": v(42.88, 93.89) * mm});
            skSolve(sketch);
        }
        {
            var Q0;
            Q0=makeQuery(id+"F94.imprint","IMPRINT",FACE,{"disambiguationData":[TD([[makeQuery(id+"F94.imprint","IMPRINT",EDGE,{"derivedFrom":sQuery(id+"F94.wireOp",EDGE,"E46.bottom")}),-1.0]])]});
            extrude(context, id + "F95", {"entities" : qUnion([Q0]), "depth" : 25.4 * mm, "offsetDistance" : 25.4 * mm});
        }
        {
            var Q0;
            Q0=qCreatedBy(makeId("Top.planeOp"),FACE);
            var sketch = newSketch(context, id + "F96", { "sketchPlane" : qUnion([Q0])});
            skLineSegment(sketch, "E48.bottom", {"start": v(4.09, 123.24) * mm, "end": v(54.89, 123.24) * mm});
            skLineSegment(sketch, "E48.top", {"start": v(4.09, 97.84) * mm, "end": v(54.89, 97.84) * mm});
            skLineSegment(sketch, "E48.left", {"start": v(4.09, 123.24) * mm, "end": v(4.09, 97.84) * mm});
            skLineSegment(sketch, "E48.right", {"start": v(54.89, 123.24) * mm, "end": v(54.89, 97.84) * mm});
            skSolve(sketch);
        }
        {
            var Q0;
            Q0=makeQuery(id+"F96.imprint","IMPRINT",FACE,{"disambiguationData":[TD([[makeQuery(id+"F96.imprint","IMPRINT",EDGE,{"derivedFrom":sQuery(id+"F96.wireOp",EDGE,"E48.bottom")}),-1.0]])]});
            extrude(context, id + "F97", {"entities" : qUnion([Q0]), "depth" : 25.4 * mm, "offsetDistance" : 25.4 * mm});
        }
        {
            var Q0;
            Q0=makeQuery(id+"F95.opExtrude","CAP_FACE",FACE,{"disambiguationData":[OSD([sQuery(id+"F94.wireOp",EDGE,"E46.bottom"),sQuery(id+"F94.wireOp",EDGE,"E46.top"),sQuery(id+"F94.wireOp",EDGE,"E46.left"),sQuery(id+"F94.wireOp",EDGE,"E46.right")])],"isStart":false});
            var sketch = newSketch(context, id + "F98", { "sketchPlane" : qUnion([Q0])});
            skCircle(sketch, "E49", {"center": v(-46.18, 110.34) * mm, "radius": 10.1 * mm});
            skSolve(sketch);
        }
        {
            var Q0;
            Q0 = qSketchRegion(id + "F98", true);
            extrude(context, id + "F99", {"entities" : qUnion([Q0]), "operationType" : NewBodyOperationType.REMOVE, "oppositeDirection" : true, "depth" : 25.4 * mm, "offsetDistance" : 25.4 * mm});
        }
        {
            var Q0;
            Q0=makeQuery(id+"F95.opExtrude","CAP_FACE",FACE,{"disambiguationData":[OSD([sQuery(id+"F94.wireOp",EDGE,"E46.bottom"),sQuery(id+"F94.wireOp",EDGE,"E46.top"),sQuery(id+"F94.wireOp",EDGE,"E46.left"),sQuery(id+"F94.wireOp",EDGE,"E46.right")])],"isStart":false});
            var sketch = newSketch(context, id + "F100", { "sketchPlane" : qUnion([Q0])});
            skText(sketch, "E50", { "text": "10.5\n", "fontName": "OpenSans-Regular.ttf"});
            const initialGuessF100  = {"E50": [-0.03558, 0.10528, 1, 0, 0.01016]};
            skSetInitialGuess(sketch, initialGuessF100);
            skSolve(sketch);
        }
        {
            var Q0;
            Q0 = qSketchRegion(id + "F100", true);
            extrude(context, id + "F101", {"entities" : qUnion([Q0]), "operationType" : NewBodyOperationType.REMOVE, "oppositeDirection" : true, "depth" : 25.4 * mm, "offsetDistance" : 25.4 * mm});
        }
        {
            var Q0;
            Q0=makeQuery(id+"F97.opExtrude","CAP_FACE",FACE,{"disambiguationData":[OSD([sQuery(id+"F96.wireOp",EDGE,"E48.bottom"),sQuery(id+"F96.wireOp",EDGE,"E48.top"),sQuery(id+"F96.wireOp",EDGE,"E48.left"),sQuery(id+"F96.wireOp",EDGE,"E48.right")])],"isStart":false});
            var sketch = newSketch(context, id + "F102", { "sketchPlane" : qUnion([Q0])});
            skCircle(sketch, "E51", {"center": v(15.66, 110.54) * mm, "radius": 10.3 * mm});
            skSolve(sketch);
        }
        {
            var Q0;
            Q0=makeQuery(id+"F102.imprint","IMPRINT",FACE,{"disambiguationData":[TD([[makeQuery(id+"F102.imprint","IMPRINT",EDGE,{"derivedFrom":sQuery(id+"F102.wireOp",EDGE,"E51")}),1.0]])]});
            extrude(context, id + "F103", {"entities" : qUnion([Q0]), "operationType" : NewBodyOperationType.REMOVE, "oppositeDirection" : true, "depth" : 25.4 * mm, "offsetDistance" : 25.4 * mm});
        }
        {
            var Q0;
            Q0=makeQuery(id+"F97.opExtrude","CAP_FACE",FACE,{"disambiguationData":[OSD([sQuery(id+"F96.wireOp",EDGE,"E48.bottom"),sQuery(id+"F96.wireOp",EDGE,"E48.top"),sQuery(id+"F96.wireOp",EDGE,"E48.left"),sQuery(id+"F96.wireOp",EDGE,"E48.right")])],"isStart":false});
            var sketch = newSketch(context, id + "F104", { "sketchPlane" : qUnion([Q0])});
            skText(sketch, "E52", { "text": "11", "fontName": "OpenSans-Regular.ttf"});
            const initialGuessF104  = {"E52": [0.03346, 0.10546, 1, 0, 0.01016]};
            skSetInitialGuess(sketch, initialGuessF104);
            skSolve(sketch);
        }
        {
            var Q0;
            Q0=makeQuery(id+"F104.imprint","IMPRINT",FACE,{"disambiguationData":[TD([[makeQuery(id+"F104.imprint","IMPRINT",EDGE,{"derivedFrom":sQuery(id+"F104.wireOp",EDGE,"E52.sketch_text.stroke-0")}),-1.0]])]});
            var Q1;
            Q1=makeQuery(id+"F104.imprint","IMPRINT",FACE,{"disambiguationData":[TD([[makeQuery(id+"F104.imprint","IMPRINT",EDGE,{"derivedFrom":sQuery(id+"F104.wireOp",EDGE,"E52.sketch_text.stroke-9")}),-1.0]])]});
            extrude(context, id + "F105", {"entities" : qUnion([Q0, Q1]), "operationType" : NewBodyOperationType.REMOVE, "oppositeDirection" : true, "depth" : 25.4 * mm, "offsetDistance" : 25.4 * mm});
        }
        {
            var Q0;
            Q0=qCreatedBy(makeId("Top.planeOp"),FACE);
            var sketch = newSketch(context, id + "F106", { "sketchPlane" : qUnion([Q0])});
            skLineSegment(sketch, "E53.bottom", {"start": v(66.56, 122.03) * mm, "end": v(117.36, 122.03) * mm});
            skLineSegment(sketch, "E53.top", {"start": v(66.56, 96.63) * mm, "end": v(117.36, 96.63) * mm});
            skLineSegment(sketch, "E53.left", {"start": v(66.56, 122.03) * mm, "end": v(66.56, 96.63) * mm});
            skLineSegment(sketch, "E53.right", {"start": v(117.36, 122.03) * mm, "end": v(117.36, 96.63) * mm});
            skSolve(sketch);
        }
        {
            var Q0;
            Q0=makeQuery(id+"F106.imprint","IMPRINT",FACE,{"disambiguationData":[TD([[makeQuery(id+"F106.imprint","IMPRINT",EDGE,{"derivedFrom":sQuery(id+"F106.wireOp",EDGE,"E53.bottom")}),-1.0]])]});
            extrude(context, id + "F107", {"entities" : qUnion([Q0]), "depth" : 25.4 * mm, "offsetDistance" : 25.4 * mm});
        }
        {
            var Q0;
            Q0=makeQuery(id+"F107.opExtrude","CAP_FACE",FACE,{"disambiguationData":[OSD([sQuery(id+"F106.wireOp",EDGE,"E53.bottom"),sQuery(id+"F106.wireOp",EDGE,"E53.top"),sQuery(id+"F106.wireOp",EDGE,"E53.left"),sQuery(id+"F106.wireOp",EDGE,"E53.right")])],"isStart":false});
            var sketch = newSketch(context, id + "F108", { "sketchPlane" : qUnion([Q0])});
            skCircle(sketch, "E54", {"center": v(78.33, 109.33) * mm, "radius": 10.5 * mm});
            skSolve(sketch);
        }
        {
            var Q0;
            Q0=makeQuery(id+"F108.imprint","IMPRINT",FACE,{"disambiguationData":[TD([[makeQuery(id+"F108.imprint","IMPRINT",EDGE,{"derivedFrom":sQuery(id+"F108.wireOp",EDGE,"E54")}),1.0]])]});
            extrude(context, id + "F109", {"entities" : qUnion([Q0]), "operationType" : NewBodyOperationType.REMOVE, "oppositeDirection" : true, "depth" : 25.4 * mm, "offsetDistance" : 25.4 * mm});
        }
        {
            var Q0;
            Q0=makeQuery(id+"F107.opExtrude","CAP_FACE",FACE,{"disambiguationData":[OSD([sQuery(id+"F106.wireOp",EDGE,"E53.bottom"),sQuery(id+"F106.wireOp",EDGE,"E53.top"),sQuery(id+"F106.wireOp",EDGE,"E53.left"),sQuery(id+"F106.wireOp",EDGE,"E53.right")])],"isStart":false});
            var sketch = newSketch(context, id + "F110", { "sketchPlane" : qUnion([Q0])});
            skText(sketch, "E55", { "text": "11.5", "fontName": "OpenSans-Regular.ttf"});
            const initialGuessF110  = {"E55": [0.08904, 0.10425, 1, 0, 0.01016]};
            skSetInitialGuess(sketch, initialGuessF110);
            skSolve(sketch);
        }
        {
            var Q0;
            Q0 = qSketchRegion(id + "F110", true);
            extrude(context, id + "F111", {"entities" : qUnion([Q0]), "operationType" : NewBodyOperationType.REMOVE, "oppositeDirection" : true, "depth" : 25.4 * mm, "offsetDistance" : 25.4 * mm});
        }
        {
            var Q0;
            Q0=qCreatedBy(makeId("Top.planeOp"),FACE);
            var sketch = newSketch(context, id + "F112", { "sketchPlane" : qUnion([Q0])});
            skLineSegment(sketch, "E56.bottom", {"start": v(107.95, 87.82) * mm, "end": v(158.75, 87.82) * mm});
            skLineSegment(sketch, "E56.top", {"start": v(107.95, 62.42) * mm, "end": v(158.75, 62.42) * mm});
            skLineSegment(sketch, "E56.left", {"start": v(107.95, 87.82) * mm, "end": v(107.95, 62.42) * mm});
            skLineSegment(sketch, "E56.right", {"start": v(158.75, 87.82) * mm, "end": v(158.75, 62.42) * mm});
            skSolve(sketch);
        }
        {
            var Q0;
            Q0=makeQuery(id+"F112.imprint","IMPRINT",FACE,{"disambiguationData":[TD([[makeQuery(id+"F112.imprint","IMPRINT",EDGE,{"derivedFrom":sQuery(id+"F112.wireOp",EDGE,"E56.bottom")}),-1.0]])]});
            extrude(context, id + "F113", {"entities" : qUnion([Q0]), "depth" : 25.4 * mm, "offsetDistance" : 25.4 * mm});
        }
        {
            var Q0;
            Q0=qCreatedBy(makeId("Top.planeOp"),FACE);
            var sketch = newSketch(context, id + "F114", { "sketchPlane" : qUnion([Q0])});
            skLineSegment(sketch, "E57.bottom", {"start": v(108.38, 51.56) * mm, "end": v(159.18, 51.56) * mm});
            skLineSegment(sketch, "E57.top", {"start": v(108.38, 26.16) * mm, "end": v(159.18, 26.16) * mm});
            skLineSegment(sketch, "E57.left", {"start": v(108.38, 51.56) * mm, "end": v(108.38, 26.16) * mm});
            skLineSegment(sketch, "E57.right", {"start": v(159.18, 51.56) * mm, "end": v(159.18, 26.16) * mm});
            skSolve(sketch);
        }
        {
            var Q0;
            Q0 = qSketchRegion(id + "F114", true);
            extrude(context, id + "F115", {"entities" : qUnion([Q0]), "depth" : 25.4 * mm, "offsetDistance" : 25.4 * mm});
        }
        {
            var Q0;
            Q0=qCreatedBy(makeId("Top.planeOp"),FACE);
            var sketch = newSketch(context, id + "F116", { "sketchPlane" : qUnion([Q0])});
            skLineSegment(sketch, "E58.bottom", {"start": v(110.9, 8.36) * mm, "end": v(161.7, 8.36) * mm});
            skLineSegment(sketch, "E58.top", {"start": v(110.9, -17.04) * mm, "end": v(161.7, -17.04) * mm});
            skLineSegment(sketch, "E58.left", {"start": v(110.9, 8.36) * mm, "end": v(110.9, -17.04) * mm});
            skLineSegment(sketch, "E58.right", {"start": v(161.7, 8.36) * mm, "end": v(161.7, -17.04) * mm});
            skSolve(sketch);
        }
        {
            var Q0;
            Q0=makeQuery(id+"F116.imprint","IMPRINT",FACE,{"disambiguationData":[TD([[makeQuery(id+"F116.imprint","IMPRINT",EDGE,{"derivedFrom":sQuery(id+"F116.wireOp",EDGE,"E58.bottom")}),-1.0]])]});
            extrude(context, id + "F117", {"entities" : qUnion([Q0]), "depth" : 25.4 * mm, "offsetDistance" : 25.4 * mm});
        }
        {
            var Q0;
            Q0=qCreatedBy(makeId("Top.planeOp"),FACE);
            var sketch = newSketch(context, id + "F118", { "sketchPlane" : qUnion([Q0])});
            skLineSegment(sketch, "E59.bottom", {"start": v(110.82, -34.76) * mm, "end": v(161.62, -34.76) * mm});
            skLineSegment(sketch, "E59.top", {"start": v(110.82, -60.16) * mm, "end": v(161.62, -60.16) * mm});
            skLineSegment(sketch, "E59.left", {"start": v(110.82, -34.76) * mm, "end": v(110.82, -60.16) * mm});
            skLineSegment(sketch, "E59.right", {"start": v(161.62, -34.76) * mm, "end": v(161.62, -60.16) * mm});
            skSolve(sketch);
        }
        {
            var Q0;
            Q0 = qSketchRegion(id + "F118", true);
            extrude(context, id + "F119", {"entities" : qUnion([Q0]), "depth" : 25.4 * mm, "offsetDistance" : 25.4 * mm});
        }
        {
            var Q0;
            Q0=makeQuery(id+"F113.opExtrude","CAP_FACE",FACE,{"disambiguationData":[OSD([sQuery(id+"F112.wireOp",EDGE,"E56.bottom"),sQuery(id+"F112.wireOp",EDGE,"E56.top"),sQuery(id+"F112.wireOp",EDGE,"E56.left"),sQuery(id+"F112.wireOp",EDGE,"E56.right")])],"isStart":false});
            var sketch = newSketch(context, id + "F120", { "sketchPlane" : qUnion([Q0])});
            skCircle(sketch, "E60", {"center": v(119.92, 75.11) * mm, "radius": 10.7 * mm});
            skSolve(sketch);
        }
        {
            var Q0;
            Q0 = qSketchRegion(id + "F120", true);
            extrude(context, id + "F121", {"entities" : qUnion([Q0]), "operationType" : NewBodyOperationType.REMOVE, "oppositeDirection" : true, "depth" : 25.4 * mm, "offsetDistance" : 25.4 * mm});
        }
        {
            var Q0;
            Q0=makeQuery(id+"F113.opExtrude","CAP_FACE",FACE,{"disambiguationData":[OSD([sQuery(id+"F112.wireOp",EDGE,"E56.bottom"),sQuery(id+"F112.wireOp",EDGE,"E56.top"),sQuery(id+"F112.wireOp",EDGE,"E56.left"),sQuery(id+"F112.wireOp",EDGE,"E56.right")])],"isStart":false});
            var sketch = newSketch(context, id + "F122", { "sketchPlane" : qUnion([Q0])});
            skText(sketch, "E61", { "text": "12", "fontName": "OpenSans-Regular.ttf"});
            const initialGuessF122  = {"E61": [0.13654, 0.07004, 1, 0, 0.01016]};
            skSetInitialGuess(sketch, initialGuessF122);
            skSolve(sketch);
        }
        {
            var Q0;
            Q0 = qSketchRegion(id + "F122", true);
            extrude(context, id + "F123", {"entities" : qUnion([Q0]), "operationType" : NewBodyOperationType.REMOVE, "oppositeDirection" : true, "depth" : 25.4 * mm, "offsetDistance" : 25.4 * mm});
        }
        {
            var Q0;
            Q0=makeQuery(id+"F115.opExtrude","CAP_FACE",FACE,{"disambiguationData":[OSD([sQuery(id+"F114.wireOp",EDGE,"E57.bottom"),sQuery(id+"F114.wireOp",EDGE,"E57.top"),sQuery(id+"F114.wireOp",EDGE,"E57.left"),sQuery(id+"F114.wireOp",EDGE,"E57.right")])],"isStart":false});
            var sketch = newSketch(context, id + "F124", { "sketchPlane" : qUnion([Q0])});
            skCircle(sketch, "E62", {"center": v(120.55, 38.86) * mm, "radius": 10.9 * mm});
            skSolve(sketch);
        }
        {
            var Q0;
            Q0=makeQuery(id+"F124.imprint","IMPRINT",FACE,{"disambiguationData":[TD([[makeQuery(id+"F124.imprint","IMPRINT",EDGE,{"derivedFrom":sQuery(id+"F124.wireOp",EDGE,"E62")}),1.0]])]});
            extrude(context, id + "F125", {"entities" : qUnion([Q0]), "operationType" : NewBodyOperationType.ADD, "depth" : 25.4 * mm, "offsetDistance" : 25.4 * mm});
        }
        {
            var Q0;
            Q0=makeQuery(id+"F125.opExtrude","CAP_FACE",FACE,{"disambiguationData":[OSD([sQuery(id+"F124.wireOp",EDGE,"E62")])],"isStart":false});
            extrude(context, id + "F126", {"entities" : qUnion([Q0]), "operationType" : NewBodyOperationType.REMOVE, "oppositeDirection" : true, "depth" : 50.8 * mm, "offsetDistance" : 25.4 * mm});
        }
        {
            var Q0;
            Q0=makeQuery(id+"F115.opExtrude","CAP_FACE",FACE,{"disambiguationData":[OSD([sQuery(id+"F114.wireOp",EDGE,"E57.bottom"),sQuery(id+"F114.wireOp",EDGE,"E57.top"),sQuery(id+"F114.wireOp",EDGE,"E57.left"),sQuery(id+"F114.wireOp",EDGE,"E57.right")])],"isStart":false});
            var sketch = newSketch(context, id + "F127", { "sketchPlane" : qUnion([Q0])});
            skText(sketch, "E63", { "text": "12.5\n", "fontName": "OpenSans-Regular.ttf"});
            const initialGuessF127  = {"E63": [0.13112, 0.03378, 1, 0, 0.01016]};
            skSetInitialGuess(sketch, initialGuessF127);
            skSolve(sketch);
        }
        {
            var Q0;
            Q0 = qSketchRegion(id + "F127", true);
            extrude(context, id + "F128", {"entities" : qUnion([Q0]), "operationType" : NewBodyOperationType.REMOVE, "oppositeDirection" : true, "depth" : 25.4 * mm, "offsetDistance" : 25.4 * mm});
        }
        {
            var Q0;
            Q0=makeQuery(id+"F117.opExtrude","CAP_FACE",FACE,{"disambiguationData":[OSD([sQuery(id+"F116.wireOp",EDGE,"E58.bottom"),sQuery(id+"F116.wireOp",EDGE,"E58.top"),sQuery(id+"F116.wireOp",EDGE,"E58.left"),sQuery(id+"F116.wireOp",EDGE,"E58.right")])],"isStart":false});
            var sketch = newSketch(context, id + "F129", { "sketchPlane" : qUnion([Q0])});
            skCircle(sketch, "E64", {"center": v(123.26, -4.34) * mm, "radius": 11.1 * mm});
            skSolve(sketch);
        }
        {
            var Q0;
            Q0=makeQuery(id+"F129.imprint","IMPRINT",FACE,{"disambiguationData":[TD([[makeQuery(id+"F129.imprint","IMPRINT",EDGE,{"derivedFrom":sQuery(id+"F129.wireOp",EDGE,"E64")}),1.0]])]});
            extrude(context, id + "F130", {"entities" : qUnion([Q0]), "operationType" : NewBodyOperationType.REMOVE, "oppositeDirection" : true, "depth" : 25.4 * mm, "offsetDistance" : 25.4 * mm});
        }
        {
            var Q0;
            Q0=makeQuery(id+"F117.opExtrude","CAP_FACE",FACE,{"disambiguationData":[OSD([sQuery(id+"F116.wireOp",EDGE,"E58.bottom"),sQuery(id+"F116.wireOp",EDGE,"E58.top"),sQuery(id+"F116.wireOp",EDGE,"E58.left"),sQuery(id+"F116.wireOp",EDGE,"E58.right")])],"isStart":false});
            var sketch = newSketch(context, id + "F131", { "sketchPlane" : qUnion([Q0])});
            skText(sketch, "E65", { "text": "13", "fontName": "OpenSans-Regular.ttf"});
            const initialGuessF131  = {"E65": [0.1399, -0.00942, 1, 0, 0.01016]};
            skSetInitialGuess(sketch, initialGuessF131);
            skSolve(sketch);
        }
        {
            var Q0;
            Q0 = qSketchRegion(id + "F131", true);
            extrude(context, id + "F132", {"entities" : qUnion([Q0]), "operationType" : NewBodyOperationType.REMOVE, "oppositeDirection" : true, "depth" : 25.4 * mm, "offsetDistance" : 25.4 * mm});
        }
        {
            var Q0;
            Q0=makeQuery(id+"F119.opExtrude","CAP_FACE",FACE,{"disambiguationData":[OSD([sQuery(id+"F118.wireOp",EDGE,"E59.bottom"),sQuery(id+"F118.wireOp",EDGE,"E59.top"),sQuery(id+"F118.wireOp",EDGE,"E59.left"),sQuery(id+"F118.wireOp",EDGE,"E59.right")])],"isStart":false});
            var sketch = newSketch(context, id + "F133", { "sketchPlane" : qUnion([Q0])});
            skCircle(sketch, "E66", {"center": v(123.39, -47.47) * mm, "radius": 11.3 * mm});
            skSolve(sketch);
        }
        {
            var Q0;
            Q0=makeQuery(id+"F133.imprint","IMPRINT",FACE,{"disambiguationData":[TD([[makeQuery(id+"F133.imprint","IMPRINT",EDGE,{"derivedFrom":sQuery(id+"F133.wireOp",EDGE,"E66")}),1.0]])]});
            extrude(context, id + "F134", {"entities" : qUnion([Q0]), "operationType" : NewBodyOperationType.REMOVE, "oppositeDirection" : true, "depth" : 25.4 * mm, "offsetDistance" : 25.4 * mm});
        }
        {
            var Q0;
            Q0=makeQuery(id+"F119.opExtrude","CAP_FACE",FACE,{"disambiguationData":[OSD([sQuery(id+"F118.wireOp",EDGE,"E59.bottom"),sQuery(id+"F118.wireOp",EDGE,"E59.top"),sQuery(id+"F118.wireOp",EDGE,"E59.left"),sQuery(id+"F118.wireOp",EDGE,"E59.right")])],"isStart":false});
            var sketch = newSketch(context, id + "F135", { "sketchPlane" : qUnion([Q0])});
            skText(sketch, "E67", { "text": "13.5\n", "fontName": "OpenSans-Regular.ttf"});
            const initialGuessF135  = {"E67": [0.13355, -0.05254, 1, 0, 0.01016]};
            skSetInitialGuess(sketch, initialGuessF135);
            skSolve(sketch);
        }
        {
            var Q0;
            Q0 = qSketchRegion(id + "F135", true);
            extrude(context, id + "F136", {"entities" : qUnion([Q0]), "operationType" : NewBodyOperationType.REMOVE, "oppositeDirection" : true, "depth" : 25.4 * mm, "offsetDistance" : 25.4 * mm});
        }
    });
